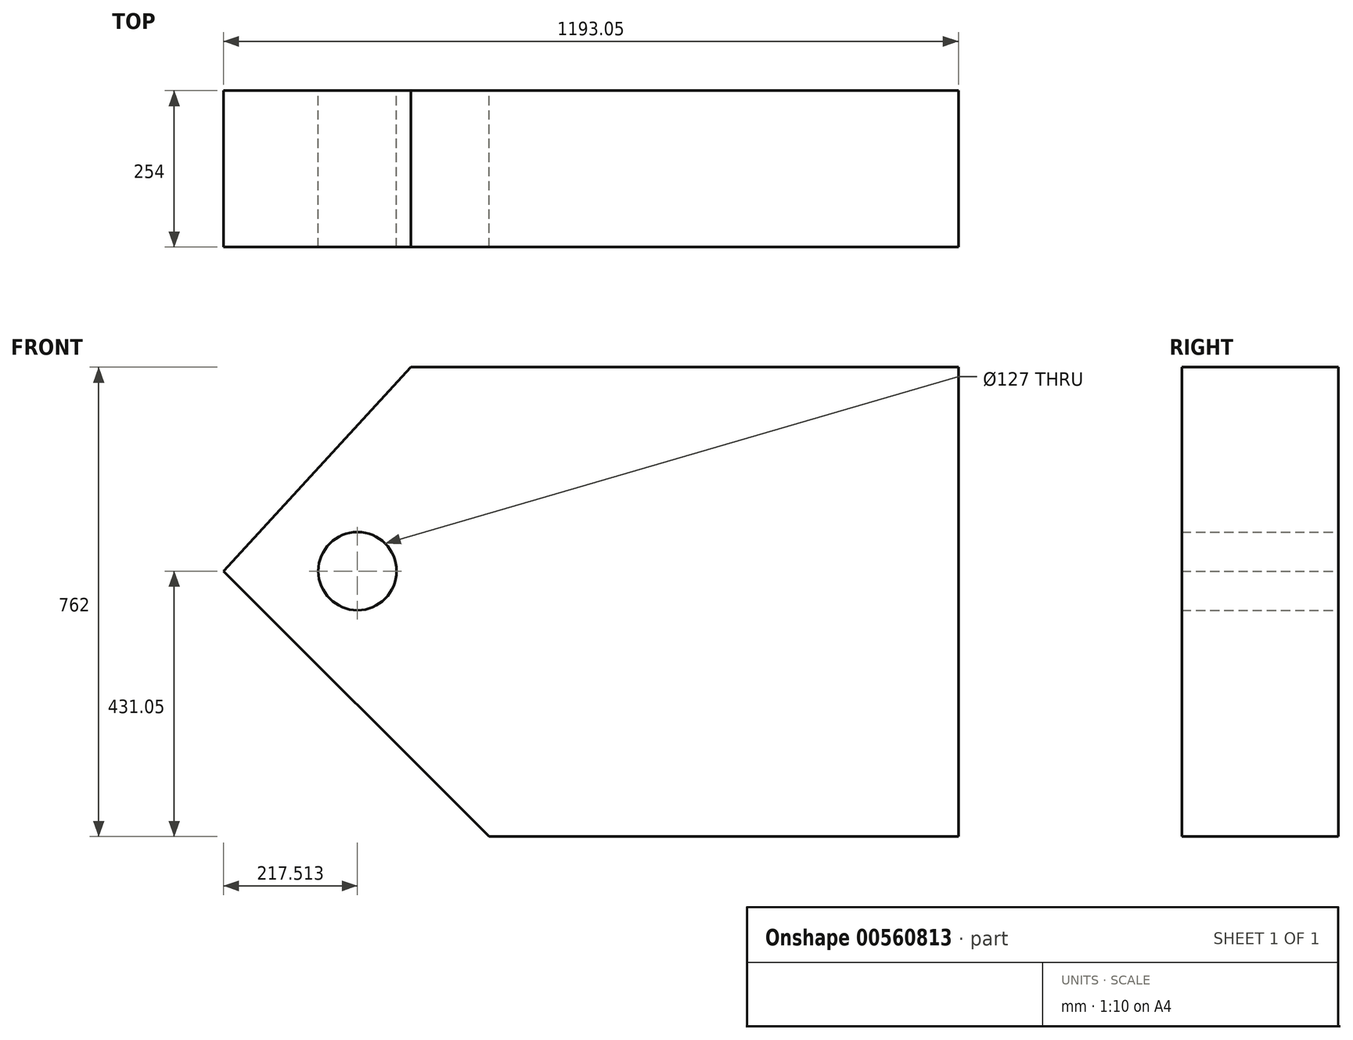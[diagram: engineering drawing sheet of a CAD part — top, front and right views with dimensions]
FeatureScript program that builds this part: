
annotation { "Feature Type Name" : "Feature", "Feature Type Description" : "" }
export const myFeature = defineFeature(function(context is Context, id is Id, definition is map)
    precondition{}
    {
        {
            var Q0;
            Q0=qCreatedBy(makeId("Front.planeOp"),FACE);
            var sketch = newSketch(context, id + "F0", { "sketchPlane" : qUnion([Q0])});
            skLineSegment(sketch, "E0", {"start": v(0, 0) * mm, "end": v(431.05, -431.05) * mm});
            skLineSegment(sketch, "E1", {"start": v(431.05, -431.05) * mm, "end": v(1193.05, -431.05) * mm});
            skLineSegment(sketch, "E2", {"start": v(1193.05, -431.05) * mm, "end": v(1193.05, 330.95) * mm});
            skLineSegment(sketch, "E3", {"start": v(1193.05, 330.95) * mm, "end": v(304.05, 330.95) * mm});
            skLineSegment(sketch, "E4", {"start": v(304.05, 330.95) * mm, "end": v(0, 0) * mm});
            skCircle(sketch, "E5", {"center": v(217.51, 0) * mm, "radius": 63.5 * mm});
            skSolve(sketch);
        }
        {
            var Q0;
            Q0 = qSketchRegion(id + "F0", true);
            extrude(context, id + "F1", {"entities" : qUnion([Q0]), "depth" : 254 * mm, "offsetDistance" : 25.4 * mm});
        }
    });
